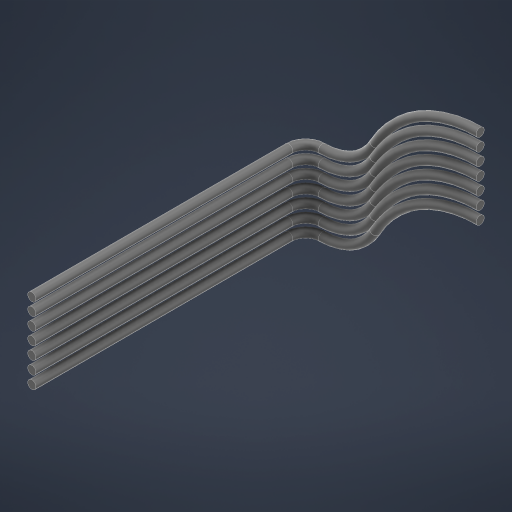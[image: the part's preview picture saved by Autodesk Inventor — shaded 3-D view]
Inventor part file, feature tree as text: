
AUTODESK INVENTOR PART (.ipt)
format: ipt  version: 2024.3 (Build 283343010, 343A)  size: 331,776 bytes
history: native  units: mm
features: sketch x3, plane x1, sweep x1, pattern_linear x1
ambient origin geometry x8: Origin, YZ Plane, XZ Plane, XY Plane, X Axis, Y Axis, Z Axis, Center Point
bodies: Volumenkörper1 (feature_tree)
feature tree (6):
  sketch  "Skizze1"  dims[d0=4.0mm d2=64.73mm]
  sketch  "Skizze2"  dims[d3=2.0mm]
  plane  "Arbeitsebene1"
  sweep  "Sweeping1"
  pattern_linear  "Rechteckige Anordnung1"  Spacing1=21.98mm  [1 undecoded]
  sketch  "Skizze3"  dims[d4=37.28mm d5=21.98mm d6=0.0mm d7=0.0mm d8=70.0mm d10=3.0mm]
note: 1 required parameter value undecoded (feature->parameter linkage not recoverable at this tier; creation-order binding heuristic only, values carry confidence <= 0.55)
